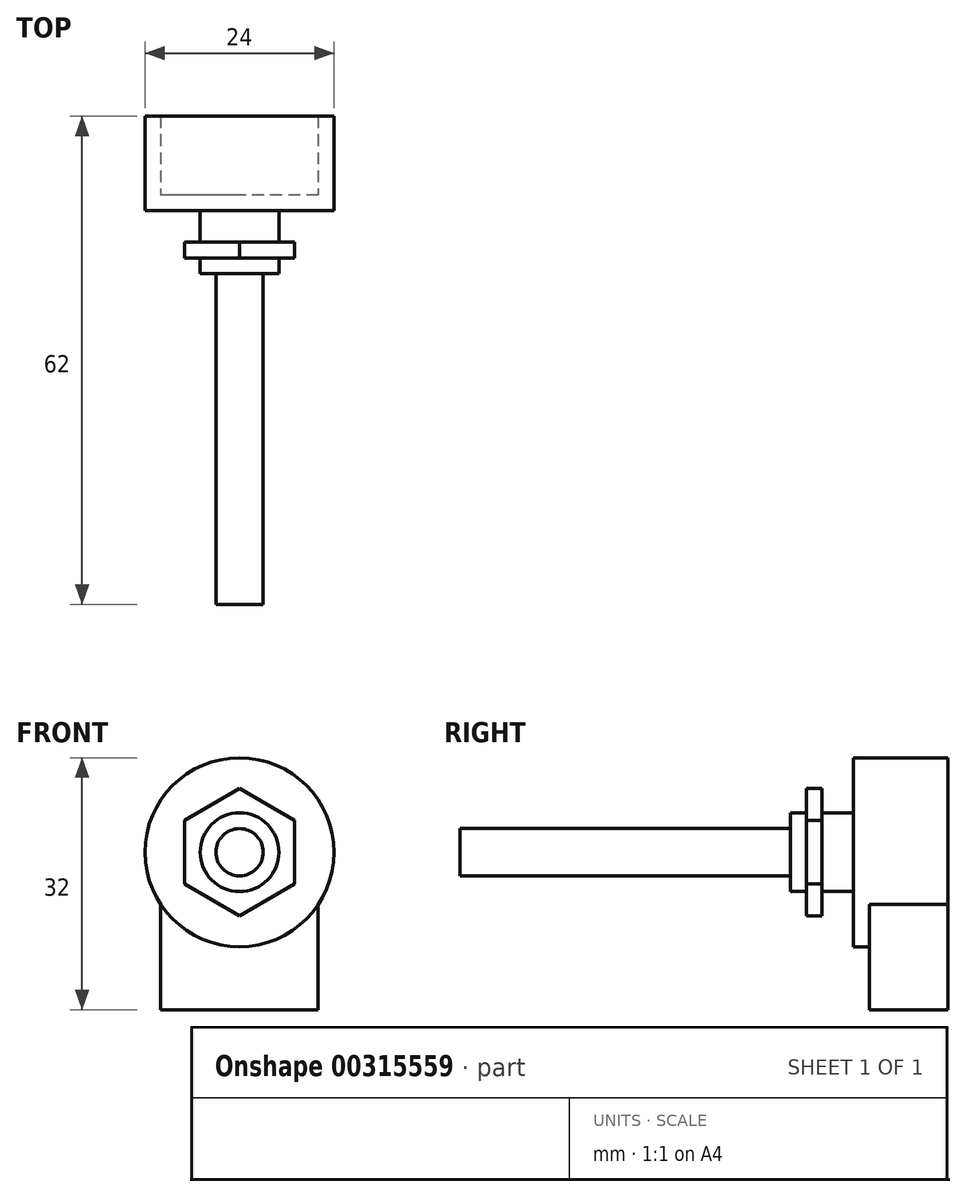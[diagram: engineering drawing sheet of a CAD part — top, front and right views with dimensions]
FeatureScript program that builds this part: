
annotation { "Feature Type Name" : "Feature", "Feature Type Description" : "" }
export const myFeature = defineFeature(function(context is Context, id is Id, definition is map)
    precondition{}
    {
        {
            var Q0;
            Q0=qCreatedBy(makeId("Front.planeOp"),FACE);
            var sketch = newSketch(context, id + "F0", { "sketchPlane" : qUnion([Q0])});
            skCircle(sketch, "E0", {"center": v(0, 0) * mm, "radius": 5 * mm});
            skSolve(sketch);
        }
        {
            var Q0;
            Q0 = qSketchRegion(id + "F0", true);
            extrude(context, id + "F1", {"entities" : qUnion([Q0]), "depth" : 8 * mm});
        }
        {
            var Q0;
            Q0=makeQuery(id+"F1.opExtrude","CAP_FACE",FACE,{"disambiguationData":[OSD([sQuery(id+"F0.wireOp",EDGE,"E0")])],"isStart":false});
            var sketch = newSketch(context, id + "F2", { "sketchPlane" : qUnion([Q0])});
            skCircle(sketch, "E1", {"center": v(0, 0) * mm, "radius": 3 * mm});
            skSolve(sketch);
        }
        {
            var Q0;
            Q0 = qSketchRegion(id + "F2", true);
            extrude(context, id + "F3", {"entities" : qUnion([Q0]), "operationType" : NewBodyOperationType.ADD, "depth" : 42 * mm});
        }
        {
            var Q0;
            Q0=qCreatedBy(makeId("Front.planeOp"),FACE);
            var sketch = newSketch(context, id + "F4", { "sketchPlane" : qUnion([Q0])});
            skCircle(sketch, "E2", {"center": v(0, 0) * mm, "radius": 12 * mm});
            skSolve(sketch);
        }
        {
            var Q0;
            Q0 = qSketchRegion(id + "F4", true);
            extrude(context, id + "F5", {"entities" : qUnion([Q0]), "operationType" : NewBodyOperationType.ADD, "oppositeDirection" : true, "depth" : 12 * mm});
        }
        {
            var Q0;
            Q0=makeQuery(id+"F5.opExtrude","CAP_FACE",FACE,{"disambiguationData":[OSD([sQuery(id+"F4.wireOp",EDGE,"E2")])],"isStart":false});
            var sketch = newSketch(context, id + "F6", { "sketchPlane" : qUnion([Q0])});
            skLineSegment(sketch, "E3.bottom", {"start": v(-10, 0) * mm, "end": v(10, 0) * mm});
            skLineSegment(sketch, "E3.top", {"start": v(-10, -20) * mm, "end": v(10, -20) * mm});
            skLineSegment(sketch, "E3.left", {"start": v(-10, 0) * mm, "end": v(-10, -20) * mm});
            skLineSegment(sketch, "E3.right", {"start": v(10, 0) * mm, "end": v(10, -20) * mm});
            skLineSegment(sketch, "E4", {"start": v(0, 0) * mm, "end": v(0, -20) * mm, "construction": true});
            skSolve(sketch);
        }
        {
            var Q0;
            Q0 = qSketchRegion(id + "F6", true);
            extrude(context, id + "F7", {"entities" : qUnion([Q0]), "operationType" : NewBodyOperationType.ADD, "oppositeDirection" : true, "depth" : 10 * mm});
        }
        {
            var Q0;
            Q0=makeQuery(id+"F1.opExtrude","CAP_FACE",FACE,{"disambiguationData":[OSD([sQuery(id+"F0.wireOp",EDGE,"E0")])],"isStart":false});
            cPlane(context, id + "F8", {"entities" : qUnion([Q0]), "cplaneType" : CPlaneType.OFFSET, "offset" : 2 * mm, "oppositeDirection" : true, "width" : 150 * mm, "height" : 150 * mm});
        }
        {
            var Q0;
            Q0=qCreatedBy(id+"F8.planeOp",FACE);
            var sketch = newSketch(context, id + "F9", { "sketchPlane" : qUnion([Q0])});
            skCircle(sketch, "E5.cCircle", {"center": v(0, 0) * mm, "radius": 7 * mm, "construction": true});
            skLineSegment(sketch, "E5.0", {"start": v(7, 4.04) * mm, "end": v(7, -4.04) * mm});
            skLineSegment(sketch, "E5.1", {"start": v(7, -4.04) * mm, "end": v(0, -8.08) * mm});
            skLineSegment(sketch, "E5.2", {"start": v(0, -8.08) * mm, "end": v(-7, -4.04) * mm});
            skLineSegment(sketch, "E5.3", {"start": v(-7, -4.04) * mm, "end": v(-7, 4.04) * mm});
            skLineSegment(sketch, "E5.4", {"start": v(-7, 4.04) * mm, "end": v(0, 8.08) * mm});
            skLineSegment(sketch, "E5.5", {"start": v(0, 8.08) * mm, "end": v(7, 4.04) * mm});
            skPoint(sketch, "E5.0.midPoint", {"position": v(7, 0) * mm});
            skSolve(sketch);
        }
        {
            var Q0;
            Q0 = qSketchRegion(id + "F9", true);
            extrude(context, id + "F10", {"entities" : qUnion([Q0]), "operationType" : NewBodyOperationType.ADD, "oppositeDirection" : true, "depth" : 2 * mm});
        }
    });
